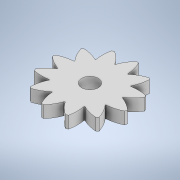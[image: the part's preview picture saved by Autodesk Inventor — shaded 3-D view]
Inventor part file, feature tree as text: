
AUTODESK INVENTOR PART (.ipt)
format: ipt  version: 2020 (Build 240168000, 168)  size: 178,176 bytes
history: native  units: in
note: dims shown in document units (in); Inventor stores cm internally (conversion verified against a paired STEP export)
features: extrude x2, sketch x2, pattern_circular x1
ambient origin geometry x8: Origin, YZ Plane, XZ Plane, XY Plane, X Axis, Y Axis, Z Axis, Center Point
bodies: Body1 (feature_tree)
feature tree (5):
  extrude  "Extrusion4"  Depth=1.1024in
  pattern_circular  "Circular Pattern1"  [2 undecoded]
  extrude  "Extrusion5"  Depth=0.1575in TaperAngle=360.0deg
  sketch  "Sketch5"  dims[d1=1.1811in d50=1.1024in]
  sketch  "Sketch6"  dims[d53=0.0197in d54=0.1575in d55=0.0in d56=4.7244in d57=360.0deg d59=0.2165in d60=0.1575in d61=0.0in]
note: 2 required parameter values undecoded (feature->parameter linkage not recoverable at this tier; creation-order binding heuristic only, values carry confidence <= 0.55)
